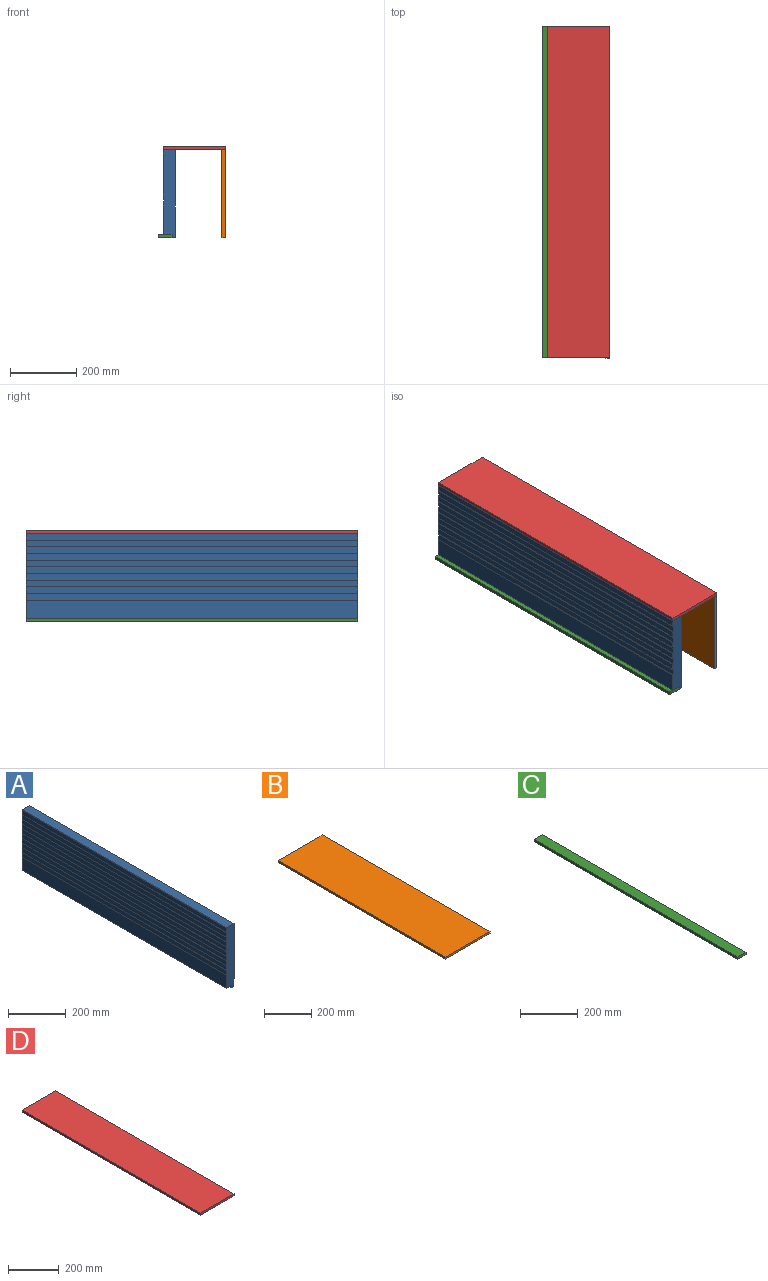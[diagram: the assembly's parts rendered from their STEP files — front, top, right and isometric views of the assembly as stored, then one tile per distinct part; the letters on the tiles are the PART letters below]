
ASSEMBLY  parts=4 mates=3
PART A: 30 faces, bbox 37x1000x266 mm
  f0: plane 266x37mm, normal (0,-1,0), area 9364.4mm2, adj f2,f3,f4,f5,f6,f7,f8,f9
  f1: plane 266x37mm, normal (0,1,0), area 9364.4mm2, adj f2,f3,f4,f5,f6,f7,f8,f9
  f2: plane 1000x1.47mm, normal (-1,0,0), area 1472.9mm2, adj f0,f1,f4,f26
  f3: plane 1000x266mm, normal (1,0,0), area 266000mm2, adj f0,f1,f26,f28
  f4: plane 1000x2mm, normal (0.45,0,0.89), area 2236.1mm2, adj f0,f1,f2,f5
  f5: plane 1000x20mm, normal (-1,0,0), area 20000mm2, adj f0,f1,f4,f6
  f6: plane 1000x2mm, normal (0.45,0,-0.89), area 2236.1mm2, adj f0,f1,f5,f7
  f7: plane 1000x22mm, normal (-1,0,0), area 22000mm2, adj f0,f1,f6,f8
  f8: plane 1000x2mm, normal (0.45,0,0.89), area 2236.1mm2, adj f0,f1,f7,f9
  f9: plane 1000x20mm, normal (-1,0,0), area 20000mm2, adj f0,f1,f8,f10
  f10: plane 1000x2mm, normal (0.45,0,-0.89), area 2236.1mm2, adj f0,f1,f9,f11
  f11: plane 1000x22mm, normal (-1,0,0), area 22000mm2, adj f0,f1,f10,f12
  f12: plane 1000x2mm, normal (0.45,0,0.89), area 2236.1mm2, adj f0,f1,f11,f13
  f13: plane 1000x20mm, normal (-1,0,0), area 20000mm2, adj f0,f1,f12,f14
  f14: plane 1000x2mm, normal (0.45,0,-0.89), area 2236.1mm2, adj f0,f1,f13,f15
  f15: plane 1000x22mm, normal (-1,0,0), area 22000mm2, adj f0,f1,f14,f16
  f16: plane 1000x2mm, normal (0.45,0,0.89), area 2236.1mm2, adj f0,f1,f15,f17
  f17: plane 1000x20mm, normal (-1,0,0), area 20000mm2, adj f0,f1,f16,f18
  f18: plane 1000x2mm, normal (0.45,0,-0.89), area 2236.1mm2, adj f0,f1,f17,f19
  f19: plane 1000x22mm, normal (-1,0,0), area 22000mm2, adj f0,f1,f18,f20
  f20: plane 1000x2mm, normal (0.45,0,0.89), area 2236.1mm2, adj f0,f1,f19,f21
  f21: plane 1000x20mm, normal (-1,0,0), area 20000mm2, adj f0,f1,f20,f22
  f22: plane 1000x2mm, normal (0.45,0,-0.89), area 2236.1mm2, adj f0,f1,f21,f23
  f23: plane 1000x22mm, normal (-1,0,0), area 22000mm2, adj f0,f1,f22,f24
  f24: plane 1000x2mm, normal (0.45,0,0.89), area 2236.1mm2, adj f0,f1,f23,f25
  f25: plane 1000x55.5mm, normal (-1,0,0), area 55503mm2, adj f0,f1,f24,f29
  f26: plane 1000x35mm, normal (0,0,1), area 35000mm2, adj f0,f1,f2,f3
  f27: plane 1000x10.02mm, normal (-1,0,0), area 10017.3mm2, adj f0,f1,f28,f29
  f28: plane 1000x10.5mm, normal (0,0,-1), area 10500mm2, adj f0,f1,f3,f27
  f29: plane 1000x26.5mm, normal (0,0,-1), area 26500mm2, adj f0,f1,f25,f27
PART B: 6 faces, bbox 266x1000x10 mm
  f0: plane 1000x10mm, normal (-1,0,0), area 10000mm2, adj f1,f3,f4,f5
  f1: plane 1000x266mm, normal (0,0,-1), area 266000mm2, adj f0,f2,f4,f5
  f2: plane 1000x10mm, normal (1,0,0), area 10000mm2, adj f1,f3,f4,f5
  f3: plane 1000x266mm, normal (0,0,1), area 266000mm2, adj f0,f2,f4,f5
  f4: plane 266x10mm, normal (0,-1,0), area 2660mm2, adj f0,f1,f2,f3
  f5: plane 266x10mm, normal (0,1,0), area 2660mm2, adj f0,f1,f2,f3
PART C: 6 faces, bbox 40x1000x10 mm
  f0: plane 1000x10mm, normal (-1,0,0), area 10000mm2, adj f1,f3,f4,f5
  f1: plane 1000x40mm, normal (0,0,-1), area 40000mm2, adj f0,f2,f4,f5
  f2: plane 1000x10mm, normal (1,0,0), area 10000mm2, adj f1,f3,f4,f5
  f3: plane 1000x40mm, normal (0,0,1), area 40000mm2, adj f0,f2,f4,f5
  f4: plane 40x10mm, normal (0,-1,0), area 400mm2, adj f0,f1,f2,f3
  f5: plane 40x10mm, normal (0,1,0), area 400mm2, adj f0,f1,f2,f3
PART D: 6 faces, bbox 187x1000x10 mm
  f0: plane 1000x10mm, normal (-1,0,0), area 10000mm2, adj f1,f3,f4,f5
  f1: plane 1000x187mm, normal (0,0,-1), area 187000mm2, adj f0,f2,f4,f5
  f2: plane 1000x10mm, normal (1,0,0), area 10000mm2, adj f1,f3,f4,f5
  f3: plane 1000x187mm, normal (0,0,1), area 187000mm2, adj f0,f2,f4,f5
  f4: plane 187x10mm, normal (0,-1,0), area 1870mm2, adj f0,f1,f2,f3
  f5: plane 187x10mm, normal (0,1,0), area 1870mm2, adj f0,f1,f2,f3
PLACE A t=(-467.39,353.04,-259.56)mm
PLACE B rot(axis=(0,1,0),90deg) t=(-430.39,353.04,195.91)mm
PLACE C t=(-620.89,353.04,-70.06)mm
PLACE D t=(-607.39,353.04,195.91)mm
MATE fastened D.f4 <-> B.f4  axis (0,-1,0) through (-420.39,-646.96,195.91)mm
MATE fastened D.f4 <-> A.f0  axis (0,-1,0) through (-605.39,-646.96,195.91)mm
MATE fastened C.f4 <-> A.f0  axis (0,-1,0) through (-580.89,-646.96,-60.06)mm
